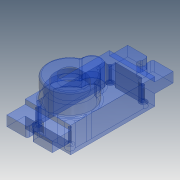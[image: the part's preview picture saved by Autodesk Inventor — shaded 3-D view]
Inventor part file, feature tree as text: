
AUTODESK INVENTOR PART (.ipt)
format: ipt  version: 2017 (Build 210142000, 142)  size: 332,288 bytes
history: native  units: mm
features: sketch x10, extrude x9, projected_geometry x8, other x1, hole x1, chamfer x1, mirror x1, fillet x1
ambient origin geometry x8: Origin, YZ Plane, XZ Plane, XY Plane, X Axis, Y Axis, Z Axis, Center Point
bodies: Body1 (feature_tree)
feature tree (32):
  other  "Твердое тело1"
  extrude  "Выдавливание1"  Depth=12.4mm
  extrude  "Выдавливание2"  Depth=23.0mm
  extrude  "Выдавливание3"  Depth=7.0mm TaperAngle=0.0deg
  hole  "Отверстие1"  [1 undecoded]
  chamfer  "Фаска1"  Distance=6.0mm
  extrude  "Выдавливание4"  Depth=9.0mm
  extrude  "Выдавливание5"  Depth=20.0mm
  extrude  "Выдавливание6"  Depth=2.0mm
  extrude  "Выдавливание7"  Depth=5.0mm TaperAngle=0.0deg
  extrude  "Выдавливание8"  Depth=0.2mm TaperAngle=45.0deg
  extrude  "Выдавливание9"  Depth=12.0mm
  mirror  "Зеркальное отражение1"
  fillet  "Сопряжение1"  Radius=5.0mm
  sketch  "Эскиз1"
  sketch  "Эскиз2"
  projected_geometry  "Спроецированная петля1"
  sketch  "Эскиз3"
  sketch  "Эскиз4"
  projected_geometry  "Спроецированная петля2"
  projected_geometry  "Спроецированная петля3"
  projected_geometry  "Спроецированная петля4"
  projected_geometry  "Спроецированная петля5"
  sketch  "Эскиз5"
  sketch  "Эскиз6"
  projected_geometry  "Спроецированная петля6"
  sketch  "Эскиз7"
  projected_geometry  "Спроецированная петля7"
  sketch  "Эскиз8"
  projected_geometry  "Спроецированная петля8"
  sketch  "Эскиз9"
  sketch  "Эскиз10"
note: 1 required parameter value undecoded (feature->parameter linkage not recoverable at this tier; creation-order binding heuristic only, values carry confidence <= 0.55)
